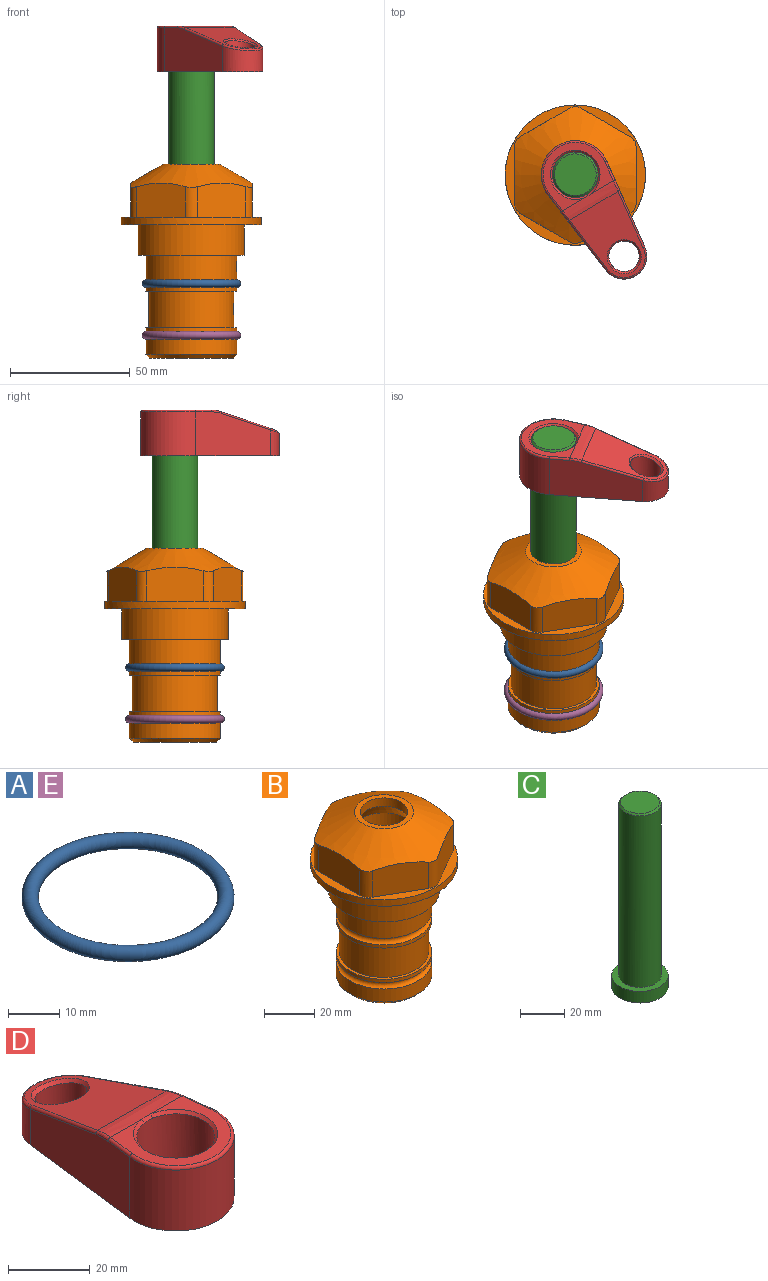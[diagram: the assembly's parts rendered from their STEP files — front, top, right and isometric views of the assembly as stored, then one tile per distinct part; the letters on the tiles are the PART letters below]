
ASSEMBLY  parts=5 mates=4
PART A: 1 faces, bbox 44.7x44.7x3.2 mm
  f0: torus R=19.05mm, axis (0,0,1), area 1193.9mm2
PART B: 36 faces, bbox 58.7x58.7x81 mm
  f0: cylinder r=17.78mm len=35.56mm, axis (0,0,1), area 1670.8mm2, adj f23,f24,f31
  f1: cylinder r=19.05mm len=38.1mm, axis (0,0,1), area 1191.9mm2, adj f26,f27,f30
  f2: plane 58.66x58.66mm, normal (0,0,-1), area 1150.6mm2, adj f3,f28
  f3: cylinder r=29.33mm len=58.66mm, axis (0,0,-1), area 585.1mm2, adj f2,f4
  f4: plane 58.66x58.66mm, normal (0,0,1), area 475.9mm2, adj f3,f5,f6,f7,f8,f9,f10,f11
  f5: plane 20.32x14.34mm, normal (-0.5,0.87,0), area 324.4mm2, adj f4,f15,f16,f17
  f6: plane 20.32x14.34mm, normal (0.5,0.87,0), area 324.4mm2, adj f4,f14,f15,f17
  f7: plane 23.48x14.34mm, normal (1,0,0), area 324.4mm2, adj f4,f13,f14,f17
  f8: plane 20.32x14.34mm, normal (0.5,-0.87,0), area 324.4mm2, adj f4,f12,f13,f17
  f9: plane 20.32x14.34mm, normal (-0.5,-0.87,0), area 324.4mm2, adj f4,f11,f12,f17
  f10: plane 23.48x14.34mm, normal (-1,0,0), area 324.4mm2, adj f4,f11,f16,f17
  f11: cylinder r=5.08mm len=12.85mm, axis (0,0,-1), area 67.2mm2, adj f4,f9,f10,f17
  f12: cylinder r=5.08mm len=12.85mm, axis (0,0,-1), area 67.2mm2, adj f4,f8,f9,f17
  f13: cylinder r=5.08mm len=12.85mm, axis (0,0,-1), area 67.2mm2, adj f4,f7,f8,f17
  f14: cylinder r=5.08mm len=12.85mm, axis (0,0,-1), area 67.2mm2, adj f4,f6,f7,f17
  f15: cylinder r=5.08mm len=12.85mm, axis (0,0,-1), area 67.2mm2, adj f4,f5,f6,f17
  f16: cylinder r=5.08mm len=12.85mm, axis (0,0,-1), area 67.2mm2, adj f4,f5,f10,f17
  f17: cone r=11.73mm half-angle=60deg, axis (0,0,-1), area 2071.8mm2, adj f5,f6,f7,f8,f9,f10,f11,f12
  f18: plane 23.46x23.46mm, normal (0,0,1), area 147.4mm2, adj f17,f35
  f19: plane 34.93x34.93mm, normal (0,0,-1), area 958mm2, adj f29
  f20: cylinder r=19.05mm len=38.1mm, axis (0,0,1), area 760.1mm2, adj f21,f29
  f21: torus R=19.05mm, axis (0,0,1), area 565.3mm2, adj f20,f22
  f22: cylinder r=19.05mm len=38.1mm, axis (0,0,1), area 190mm2, adj f21,f23
  f23: plane 38.1x38.1mm, normal (0,0,1), area 146.9mm2, adj f0,f22
  f24: plane 38.1x38.1mm, normal (0,0,-1), area 146.9mm2, adj f0,f25
  f25: cylinder r=19.05mm len=38.1mm, axis (0,0,1), area 190mm2, adj f24,f26
  f26: torus R=19.05mm, axis (0,0,1), area 565.3mm2, adj f1,f25
  f27: plane 44.45x44.45mm, normal (0,0,-1), area 411.7mm2, adj f1,f28
  f28: cylinder r=22.23mm len=44.45mm, axis (0,0,1), area 1773.5mm2, adj f2,f27
  f29: cone r=19.05mm half-angle=45deg, axis (0,0,1), area 257.5mm2, adj f19,f20
  f30: cylinder r=3.17mm len=6.75mm, axis (-1,0,0), area 128mm2, adj f1,f33
  f31: cylinder r=3.17mm len=6.35mm, axis (-1,0,0), area 102.5mm2, adj f0,f33
  f32: plane 25.4x25.4mm, normal (0,0,1), area 506.7mm2, adj f33
  f33: cylinder r=12.7mm len=66.42mm, axis (0,0,-1), area 5236.2mm2, adj f30,f31,f32,f34
  f34: cone r=9.53mm half-angle=30deg, axis (0,0,-1), area 443.4mm2, adj f33,f35
  f35: cylinder r=9.53mm len=19.05mm, axis (0,0,-1), area 240.9mm2, adj f18,f34
PART C: 6 faces, bbox 25.4x25.4x101.6 mm
  f0: plane 17.46x17.46mm, normal (0,0,1), area 239.5mm2, adj f5
  f1: plane 25.4x25.4mm, normal (0,0,-1), area 506.7mm2, adj f2
  f2: cylinder r=12.7mm len=25.4mm, axis (0,0,1), area 506.7mm2, adj f1,f3
  f3: plane 25.4x25.4mm, normal (0,0,1), area 221.7mm2, adj f2,f4
  f4: cylinder r=9.53mm len=94.46mm, axis (0,0,1), area 5653mm2, adj f3,f5
  f5: cone r=8.73mm half-angle=45deg, axis (0,0,-1), area 64.4mm2, adj f0,f4
PART D: 31 faces, bbox 31.7x65.5x19.8 mm
  f0: plane 39.12x18.26mm, normal (0.99,0.12,0), area 612.2mm2, adj f1,f4,f7,f11,f13,f15
  f1: cylinder r=9.53mm len=18.91mm, axis (0,0,-1), area 296.1mm2, adj f0,f2,f7,f17
  f2: plane 39.12x18.26mm, normal (-0.99,0.12,0), area 612.2mm2, adj f1,f4,f7,f12,f14,f16
  f3: cylinder r=6.35mm len=12.7mm, axis (0,0,-1), area 362.4mm2, adj f7,f18
  f4: cylinder r=14.29mm len=28.58mm, axis (0,0,-1), area 882.2mm2, adj f0,f2,f7,f10
  f5: cylinder r=9.53mm len=19.05mm, axis (0,0,-1), area 1092.6mm2, adj f7,f19,f20
  f6: plane 26.99x23.69mm, normal (0,0,1), area 216.2mm2, adj f9,f10,f11,f12,f19
  f7: plane 63.5x28.58mm, normal (0,0,-1), area 661.8mm2, adj f0,f1,f2,f3,f4,f5,f22,f23
  f8: plane 33.52x23.6mm, normal (0,0.26,0.97), area 486mm2, adj f9,f15,f16,f17,f18
  f9: cylinder r=19.05mm len=24.72mm, axis (1,0,0), area 120.4mm2, adj f6,f8,f13,f14,f20
  f10: torus R=13.49mm, axis (0,0,1), area 59mm2, adj f4,f6,f11,f12
  f11: cylinder r=0.79mm len=8.67mm, axis (0.12,-0.99,0), area 10.8mm2, adj f0,f6,f10,f13
  f12: cylinder r=0.79mm len=8.67mm, axis (0.12,0.99,0), area 10.8mm2, adj f2,f6,f10,f14
  f13: bspline ~4.95x1.42mm, area 6.1mm2, adj f0,f9,f11,f15
  f14: bspline ~4.95x1.42mm, area 6.1mm2, adj f2,f9,f12,f16
  f15: cylinder r=0.79mm len=25.95mm, axis (0.12,-0.96,0.26), area 32.9mm2, adj f0,f8,f13,f17
  f16: cylinder r=0.79mm len=25.95mm, axis (0.12,0.96,-0.26), area 32.9mm2, adj f2,f8,f14,f17
  f17: bspline ~18.91x8.38mm, area 30mm2, adj f1,f8,f15,f16
  f18: bspline ~14.29x14.29mm, area 48.3mm2, adj f3,f8
  f19: cone r=9.53mm half-angle=45deg, axis (0,0,1), area 66.5mm2, adj f5,f6,f20
  f20: bspline ~3.22x0.96mm, area 3.5mm2, adj f5,f9,f19
  f21: plane 2.75x2.72mm, normal (0,0,-1), area 2.9mm2, adj f23,f25,f28
  f22: plane 23.05x15.88mm, normal (-0.99,-0.12,0), area 323.6mm2, adj f7,f25,f26,f27,f28,f29
  f23: plane 23.05x15.88mm, normal (0.99,-0.12,0), area 323.6mm2, adj f7,f21,f25,f27,f28,f30
  f24: cylinder r=9.53mm len=10.69mm, axis (0,0,-1), area 114.7mm2, adj f7,f27,f29,f30
  f25: cylinder r=12.7mm len=20.59mm, axis (0,0,-1), area 381.1mm2, adj f7,f21,f22,f23,f26,f28
  f26: plane 2.75x2.72mm, normal (0,0,-1), area 2.9mm2, adj f22,f25,f28
  f27: plane 19.72x18.37mm, normal (0,-0.26,-0.97), area 291.8mm2, adj f22,f23,f24,f28,f29,f30
  f28: cylinder r=15.88mm len=19.92mm, axis (1,0,0), area 54.8mm2, adj f21,f22,f23,f25,f26,f27
  f29: cylinder r=1.59mm len=11mm, axis (0,0,-1), area 34.7mm2, adj f7,f22,f24,f27
  f30: cylinder r=1.59mm len=11mm, axis (0,0,-1), area 34.7mm2, adj f7,f23,f24,f27
PART E: same geometry as A
PLACE A t=(-42.95,-77.71,0)mm
PLACE B t=(-42.95,-77.71,0)mm fixed
PLACE C rot(axis=(0,0,-1),149.1deg) t=(-42.95,-77.71,19.7)mm
PLACE D rot(axis=(0,0,-1),149.1deg) t=(-42.95,-77.71,19.7)mm
PLACE E t=(-42.95,-77.71,-21.59)mm
MATE fastened D.f4 <-> C.f2  axis (0,0,1) through (-42.95,-77.71,83.2)mm
MATE fastened E.f0 <-> B.f0  axis (0,0,1) through (-42.95,-77.71,-46.1)mm
MATE cylindrical C.f2 <-> B.f0  axis (0,0,-1) through (-42.95,-77.71,-18.4)mm
MATE fastened A.f0 <-> B.f0  axis (0,0,1) through (-42.95,-77.71,-24.51)mm
